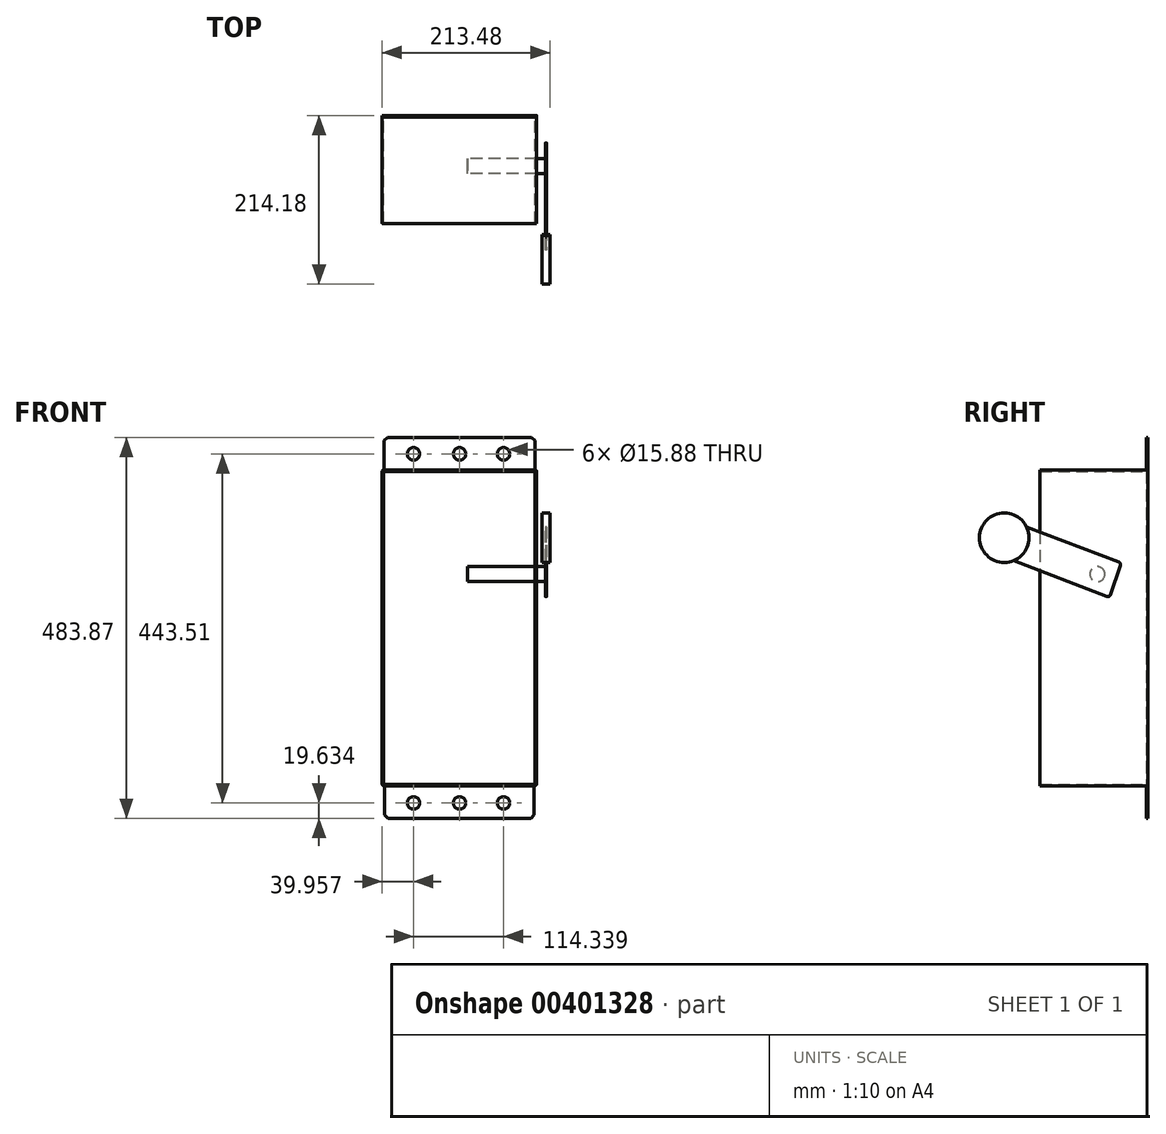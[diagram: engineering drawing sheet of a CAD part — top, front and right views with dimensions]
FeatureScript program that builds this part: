
annotation { "Feature Type Name" : "Feature", "Feature Type Description" : "" }
export const myFeature = defineFeature(function(context is Context, id is Id, definition is map)
    precondition{}
    {
        {
            var Q0;
            Q0=qCreatedBy(makeId("Front.planeOp"),FACE);
            var sketch = newSketch(context, id + "F0", { "sketchPlane" : qUnion([Q0])});
            skLineSegment(sketch, "E0.bottom", {"start": v(-194.04, 192.96) * mm, "end": v(-2, 192.96) * mm});
            skLineSegment(sketch, "E0.top", {"start": v(-193.28, -208.61) * mm, "end": v(-3.29, -208.61) * mm});
            skLineSegment(sketch, "E0.left", {"start": v(-196.46, 190.55) * mm, "end": v(-196.46, -205.44) * mm});
            skLineSegment(sketch, "E0.right", {"start": v(-0.11, 191.07) * mm, "end": v(-0.11, -205.44) * mm});
            skPoint(sketch, "E1.visualSharp", {"position": v(-0.11, 192.96) * mm});
            skArc(sketch, "E1.filletArc", {"start": v(-0.11, 191.07) * mm, "mid": v(-0.67, 192.4) * mm, "end": v(-2, 192.96) * mm});
            skPoint(sketch, "E2.visualSharp", {"position": v(-196.46, 192.96) * mm});
            skArc(sketch, "E2.filletArc", {"start": v(-194.04, 192.96) * mm, "mid": v(-195.75, 192.25) * mm, "end": v(-196.46, 190.55) * mm});
            skPoint(sketch, "E3.visualSharp", {"position": v(-0.11, -208.61) * mm});
            skArc(sketch, "E3.filletArc", {"start": v(-3.29, -208.61) * mm, "mid": v(-1.04, -207.68) * mm, "end": v(-0.11, -205.44) * mm});
            skPoint(sketch, "E4.visualSharp", {"position": v(-196.46, -208.61) * mm});
            skArc(sketch, "E4.filletArc", {"start": v(-196.46, -205.44) * mm, "mid": v(-195.53, -207.68) * mm, "end": v(-193.28, -208.61) * mm});
            skLineSegment(sketch, "E5", {"start": v(-193.28, -208.61) * mm, "end": v(-193.28, -245.54) * mm});
            skLineSegment(sketch, "E6", {"start": v(-189.06, -249.76) * mm, "end": v(-7.51, -249.76) * mm});
            skLineSegment(sketch, "E7", {"start": v(-3.29, -245.54) * mm, "end": v(-3.29, -208.61) * mm});
            skPoint(sketch, "E8.visualSharp", {"position": v(-193.28, -249.76) * mm});
            skLineSegment(sketch, "E9", {"start": v(-194.04, 192.96) * mm, "end": v(-194.04, 230.2) * mm});
            skLineSegment(sketch, "E10", {"start": v(-189.53, 234.1) * mm, "end": v(-6.46, 234.1) * mm});
            skLineSegment(sketch, "E11", {"start": v(-2, 230.13) * mm, "end": v(-2, 192.96) * mm});
            skPoint(sketch, "E12.visualSharp", {"position": v(-194.04, 234.1) * mm});
            skPoint(sketch, "E13.visualSharp", {"position": v(-2, 234.1) * mm});
            skLineSegment(sketch, "E14", {"start": v(-194.04, 230.2) * mm, "end": v(-189.53, 234.1) * mm});
            skLineSegment(sketch, "E15", {"start": v(-2, 230.13) * mm, "end": v(-6.46, 234.1) * mm});
            skLineSegment(sketch, "E16", {"start": v(-193.28, -245.54) * mm, "end": v(-189.06, -249.76) * mm});
            skLineSegment(sketch, "E17", {"start": v(-3.29, -245.54) * mm, "end": v(-7.51, -249.76) * mm});
            skCircle(sketch, "E18", {"center": v(-98, 213.38) * mm, "radius": 7.94 * mm});
            skPoint(sketch, "E18.centerSnap0", {"position": v(-98, 234.1) * mm});
            skCircle(sketch, "E19", {"center": v(-42.16, 213.38) * mm, "radius": 7.94 * mm});
            skCircle(sketch, "E20", {"center": v(-156.5, 213.38) * mm, "radius": 7.94 * mm});
            skCircle(sketch, "E21", {"center": v(-98, -230.13) * mm, "radius": 7.94 * mm});
            skCircle(sketch, "E22", {"center": v(-42.16, -230.13) * mm, "radius": 7.94 * mm});
            skCircle(sketch, "E23", {"center": v(-156.5, -230.13) * mm, "radius": 7.94 * mm});
            skSolve(sketch);
        }
        {
            var Q0;
            Q0=makeQuery(id+"F0.imprint","IMPRINT",FACE,{"disambiguationData":[TD([[makeQuery(id+"F0.imprint","IMPRINT",EDGE,{"derivedFrom":sQuery(id+"F0.wireOp",EDGE,"E0.bottom")}),-1.0]])]});
            extrude(context, id + "F1", {"entities" : qUnion([Q0]), "depth" : 137.16 * mm});
        }
        {
            var Q0;
            Q0=makeQuery(id+"F1.opExtrude","CAP_FACE",FACE,{"disambiguationData":[OSD([sQuery(id+"F0.wireOp",EDGE,"E0.bottom"),sQuery(id+"F0.wireOp",EDGE,"E0.top"),sQuery(id+"F0.wireOp",EDGE,"E0.left"),sQuery(id+"F0.wireOp",EDGE,"E0.right"),sQuery(id+"F0.wireOp",EDGE,"E1.filletArc"),sQuery(id+"F0.wireOp",EDGE,"E2.filletArc"),sQuery(id+"F0.wireOp",EDGE,"E3.filletArc"),sQuery(id+"F0.wireOp",EDGE,"E4.filletArc")])],"isStart":false});
            shell(context, id + "F2", {"entities" : qUnion([Q0]), "thickness" : 1.88 * mm});
        }
        {
            var Q0;
            Q0=makeQuery(id+"F0.imprint","IMPRINT",FACE,{"disambiguationData":[TD([[makeQuery(id+"F0.imprint","IMPRINT",EDGE,{"derivedFrom":sQuery(id+"F0.wireOp",EDGE,"E0.bottom")}),1.0]])]});
            extrude(context, id + "F3", {"entities" : qUnion([Q0]), "operationType" : NewBodyOperationType.ADD, "depth" : 1.88 * mm});
        }
        {
            var Q0;
            Q0=makeQuery(id+"F0.imprint","IMPRINT",FACE,{"disambiguationData":[TD([[makeQuery(id+"F0.imprint","IMPRINT",EDGE,{"derivedFrom":sQuery(id+"F0.wireOp",EDGE,"E0.top")}),-1.0]])]});
            extrude(context, id + "F4", {"entities" : qUnion([Q0]), "operationType" : NewBodyOperationType.ADD, "depth" : 1.88 * mm});
        }
        {
            var Q0;
            Q0=qCreatedBy(makeId("Right.planeOp"),FACE);
            var sketch = newSketch(context, id + "F5", { "sketchPlane" : qUnion([Q0])});
            skCircle(sketch, "E24", {"center": v(-64.39, 60.51) * mm, "radius": 9.53 * mm});
            skLineSegment(sketch, "E25", {"start": v(-52.1, 32.17) * mm, "end": v(-170.9, 77.63) * mm});
            skLineSegment(sketch, "E26", {"start": v(-154.43, 120.65) * mm, "end": v(-37.07, 75.73) * mm});
            skLineSegment(sketch, "E27", {"start": v(-35.2, 71.75) * mm, "end": v(-47.96, 34.11) * mm});
            skPoint(sketch, "E28.visualSharp", {"position": v(-34.21, 74.64) * mm});
            skArc(sketch, "E28.filletArc", {"start": v(-35.2, 71.75) * mm, "mid": v(-35.33, 74.12) * mm, "end": v(-37.07, 75.73) * mm});
            skPoint(sketch, "E29.visualSharp", {"position": v(-49.02, 30.99) * mm});
            skArc(sketch, "E29.filletArc", {"start": v(-52.1, 32.17) * mm, "mid": v(-49.62, 32.26) * mm, "end": v(-47.96, 34.11) * mm});
            skCircle(sketch, "E30", {"center": v(-182.7, 106.8) * mm, "radius": 31.48 * mm});
            skPoint(sketch, "E31.orphan", {"position": v(-174.47, 128.32) * mm});
            skPoint(sketch, "E32.orphan", {"position": v(-190.94, 85.3) * mm});
            skSolve(sketch);
        }
        {
            var Q0;
            Q0=makeQuery(id+"F5.imprint","IMPRINT",FACE,{"disambiguationData":[TD([[makeQuery(id+"F5.imprint","IMPRINT",EDGE,{"derivedFrom":sQuery(id+"F5.wireOp",EDGE,"E24")}),1.0]])]});
            extrude(context, id + "F6", {"entities" : qUnion([Q0]), "depth" : 12.7 * mm, "hasSecondDirection" : true, "secondDirectionOppositeDirection" : true, "secondDirectionDepth" : 87.88 * mm});
        }
        {
            var Q0;
            Q0=makeQuery(id+"F5.imprint","IMPRINT",FACE,{"disambiguationData":[TD([[makeQuery(id+"F5.imprint","IMPRINT",EDGE,{"derivedFrom":sQuery(id+"F5.wireOp",EDGE,"E24")}),-1.0]])]});
            var Q1;
            Q1=makeQuery(id+"F6.opExtrude","CAP_FACE",FACE,{"disambiguationData":[OSD([sQuery(id+"F5.wireOp",EDGE,"E24")])],"isStart":false});
            extrude(context, id + "F7", {"entities" : qUnion([Q0]), "operationType" : NewBodyOperationType.ADD, "endBound" : BoundingType.UP_TO_SURFACE, "endBoundEntityFace" : qUnion([Q1]), "depth" : 25.4 * mm, "hasSecondDirection" : true, "secondDirectionOppositeDirection" : false, "secondDirectionDepth" : 10.92 * mm});
        }
        {
            var Q0;
            {var subQ0=sQuery(id+"F5.wireOp",EDGE,"E30");var subQ1=makeQuery(id+"F5.imprint","INTERSECT",VERTEX,{"derivedFrom":[sQuery(id+"F5.wireOp",EDGE,"E25"),subQ0]});Q0=makeQuery(id+"F5.imprint","IMPRINT",FACE,{"disambiguationData":[TD([[makeQuery(id+"F5.imprint","IMPRINT",EDGE,{"disambiguationData":[TD([[subQ1,1.0]])],"derivedFrom":subQ0}),1.0]])]});}
            extrude(context, id + "F8", {"entities" : qUnion([Q0]), "operationType" : NewBodyOperationType.ADD, "depth" : 17.02 * mm, "hasSecondDirection" : true, "secondDirectionOppositeDirection" : false, "secondDirectionDepth" : 6.6 * mm});
        }
    });
